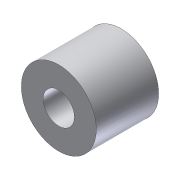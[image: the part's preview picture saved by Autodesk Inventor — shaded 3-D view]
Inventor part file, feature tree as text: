
AUTODESK INVENTOR PART (.ipt)
format: ipt  version: 2012 (Build 160160000, 160)  size: 80,896 bytes
history: native  units: in
note: dims shown in document units (in); Inventor stores cm internally (conversion verified against a paired STEP export)
features: extrude x1, sketch x1
ambient origin geometry x8: Origin, YZ Plane, XZ Plane, XY Plane, X Axis, Y Axis, Z Axis, Center Point
bodies: Solid1 (feature_tree)
feature tree (2):
  extrude  "Extrusion1"  Depth=0.625in
  sketch  "Sketch1"  dims[d0=1.5in d1=0.625in d2=1.25in d3=0.0in]
